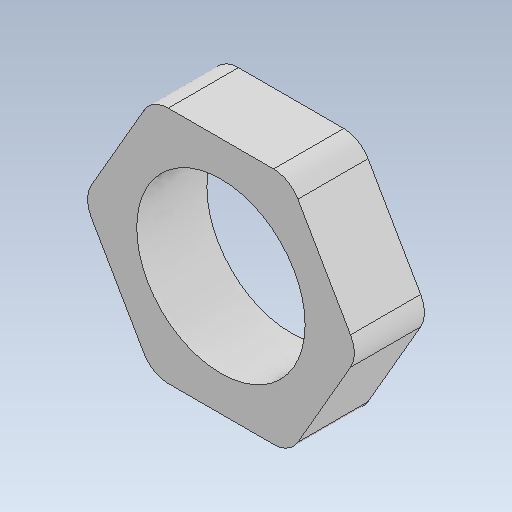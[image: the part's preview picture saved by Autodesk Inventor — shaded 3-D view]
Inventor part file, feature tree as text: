
AUTODESK INVENTOR PART (.ipt)
format: ipt  version: 2021 (Build 250183000, 183)  size: 115,712 bytes
history: native  units: mm
features: extrude x2, sketch x2, fillet x1
ambient origin geometry x8: Origin, YZ Plane, XZ Plane, XY Plane, X Axis, Y Axis, Z Axis, Center Point
bodies: Solid1 (feature_tree)
feature tree (5):
  extrude  "Extrusion1"  Depth=5.0mm TaperAngle=0.0deg
  extrude  "Extrusion2"  TaperAngle=0.0deg  [1 undecoded]
  fillet  "Fillet1"  Radius=2.0mm
  sketch  "Sketch1"  dims[d0=17.0mm d1=5.0mm d2=0.0mm]
  sketch  "Sketch2"  dims[d3=12.0mm d4=0.0mm d5=0.0mm d6=2.0mm]
note: 1 required parameter value undecoded (feature->parameter linkage not recoverable at this tier; creation-order binding heuristic only, values carry confidence <= 0.55)
